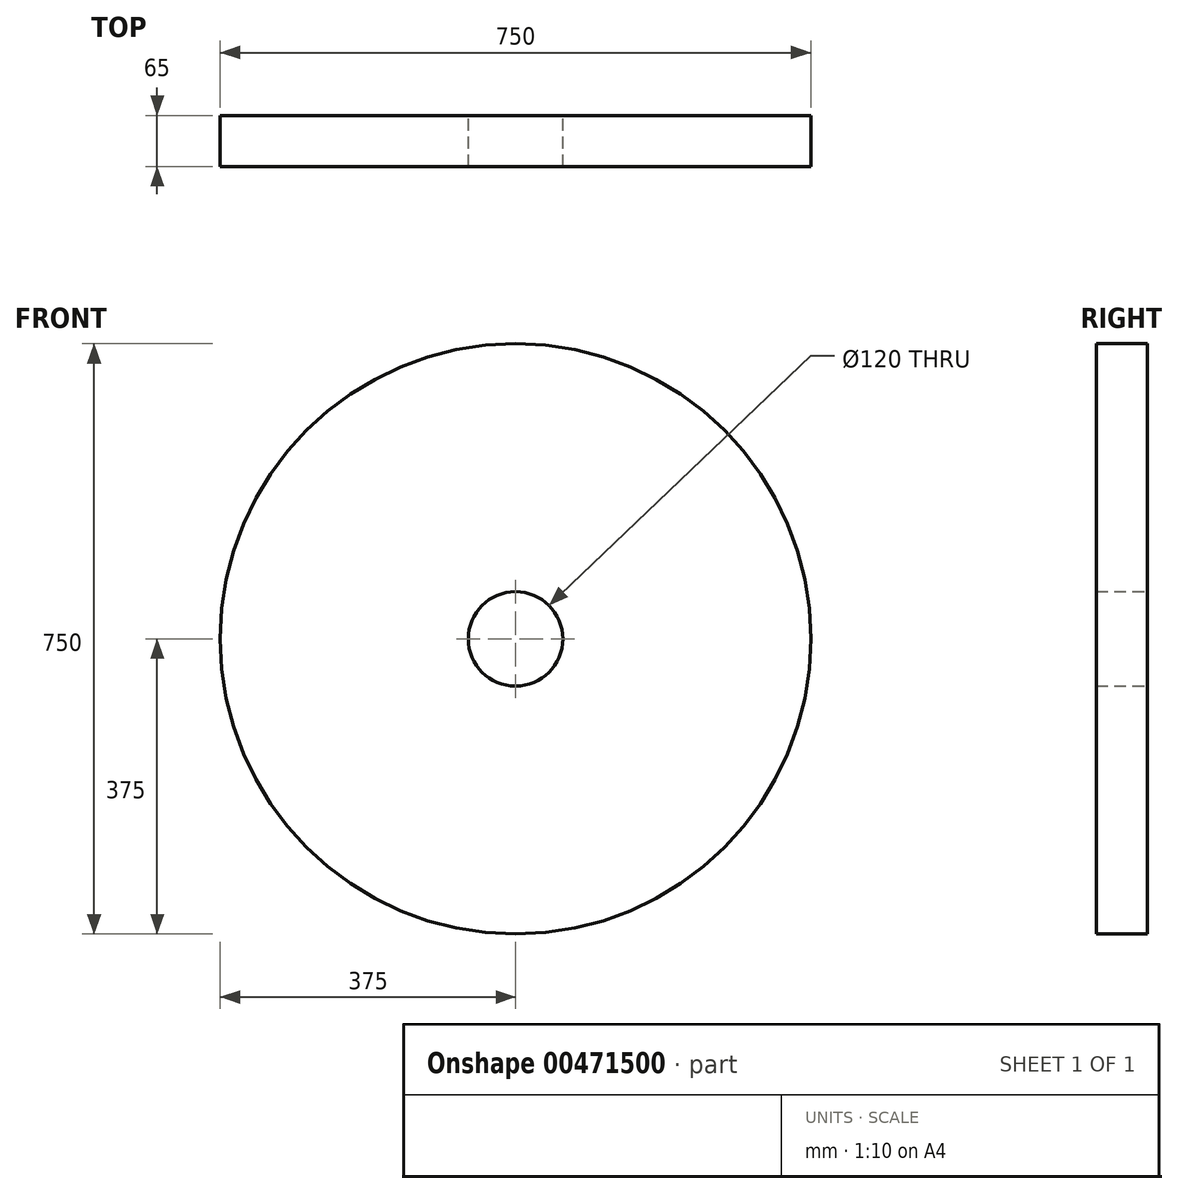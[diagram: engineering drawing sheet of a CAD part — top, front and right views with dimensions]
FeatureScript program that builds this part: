
annotation { "Feature Type Name" : "Feature", "Feature Type Description" : "" }
export const myFeature = defineFeature(function(context is Context, id is Id, definition is map)
    precondition{}
    {
        {
            var Q0;
            Q0=qCreatedBy(makeId("Front.planeOp"),FACE);
            var sketch = newSketch(context, id + "F0", { "sketchPlane" : qUnion([Q0])});
            skCircle(sketch, "E0", {"center": v(0, 0) * mm, "radius": 375 * mm});
            skCircle(sketch, "E1", {"center": v(0, 0) * mm, "radius": 60 * mm});
            skSolve(sketch);
        }
        {
            var Q0;
            Q0 = qSketchRegion(id + "F0", true);
            extrude(context, id + "F1", {"entities" : qUnion([Q0]), "depth" : 65 * mm});
        }
    });
